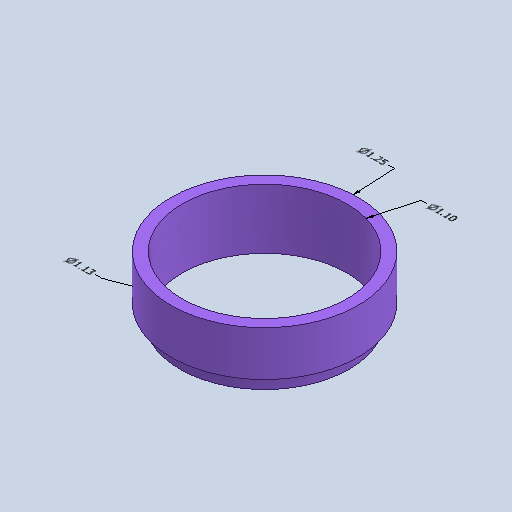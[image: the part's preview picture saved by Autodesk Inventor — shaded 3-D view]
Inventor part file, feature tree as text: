
AUTODESK INVENTOR PART (.ipt)
format: ipt  version: 2022.1 (Build 261234000, 234)  size: 129,024 bytes
history: native  units: in
note: dims shown in document units (in); Inventor stores cm internally (conversion verified against a paired STEP export)
features: other x4, revolve x1, sketch x1
ambient origin geometry x8: Origin, YZ Plane, XZ Plane, XY Plane, X Axis, Y Axis, Z Axis, Center Point
bodies: Solid1 (feature_tree)
feature tree (6):
  other  "Annotations"
  revolve  "Revolution1"  [1 undecoded]
  sketch  "Sketch1"  dims[d0=0.1in d1=0.3in d2=0.55in d3=0.625in d4=0.565in d5=90.0deg d10=0.8708in d11=1.13in d6=1.5561in d7=1.1in d8=1.6568in d9=1.25in]
  other  "Diameter Dimension 1"
  other  "Diameter Dimension 2"
  other  "Diameter Dimension 3"
note: 1 required parameter value undecoded (feature->parameter linkage not recoverable at this tier; creation-order binding heuristic only, values carry confidence <= 0.55)
